# Revit family: Enduro_4
name_source: partatom
category: Drzwi
revit_build: Autodesk Revit 2016 (Build: 20150714_1515(x64)
units: mm (PartAtom-declared; Revit-internal decimal feet)

## family parameters
Obiekt nadrzędny = Ściana
Punkt obliczania pomieszczeń = Nie
Tnij formami wycięć po wczytaniu = Nie
Współdzielony = Nie
Zawsze pionowo = Tak

## types (5) — shared parameters
Funkcja = Wewnętrzna
Hs = 2030 mm  [stored 6.6601 ft]
Informacja = Własność Porta KMI Poland, wszelkie prawa zastrzeżone.
Konstrukcja analityczna = <Brak>
Producent = PORTA KMI POLAND
URL = www.porta.com.pl
Wysokość = 2055 mm  [stored 6.74213 ft]
Zakończenie ściany = Wg obiektu nadrzędnego

## per-type parameters (varying)
| type | Promień_otwór | Sb | Ss | Szerokość |
| PN 60 | 160 mm  [stored 0.524934 ft] | 656 mm | 644 mm | 675 mm |
| PN 70 | 160 mm  [stored 0.524934 ft] | 756 mm | 744 mm | 775 mm |
| PN 80 | 189 mm | 856 mm | 844 mm | 875 mm |
| PN 90 | 189 mm | 964 mm | 952 mm  [stored 3.12336 ft] | 985 mm  [stored 3.23163 ft] |
| PN 100 | 189 mm | 1056 mm | 1044 mm | 1075 mm |

note: [stored X ft] marks values corroborated as IEEE doubles in the binary element streams (Revit-internal decimal feet)

## geometry (parser evidence)
native form markers: Blend x4
no freeform markers — native parametric forms only
